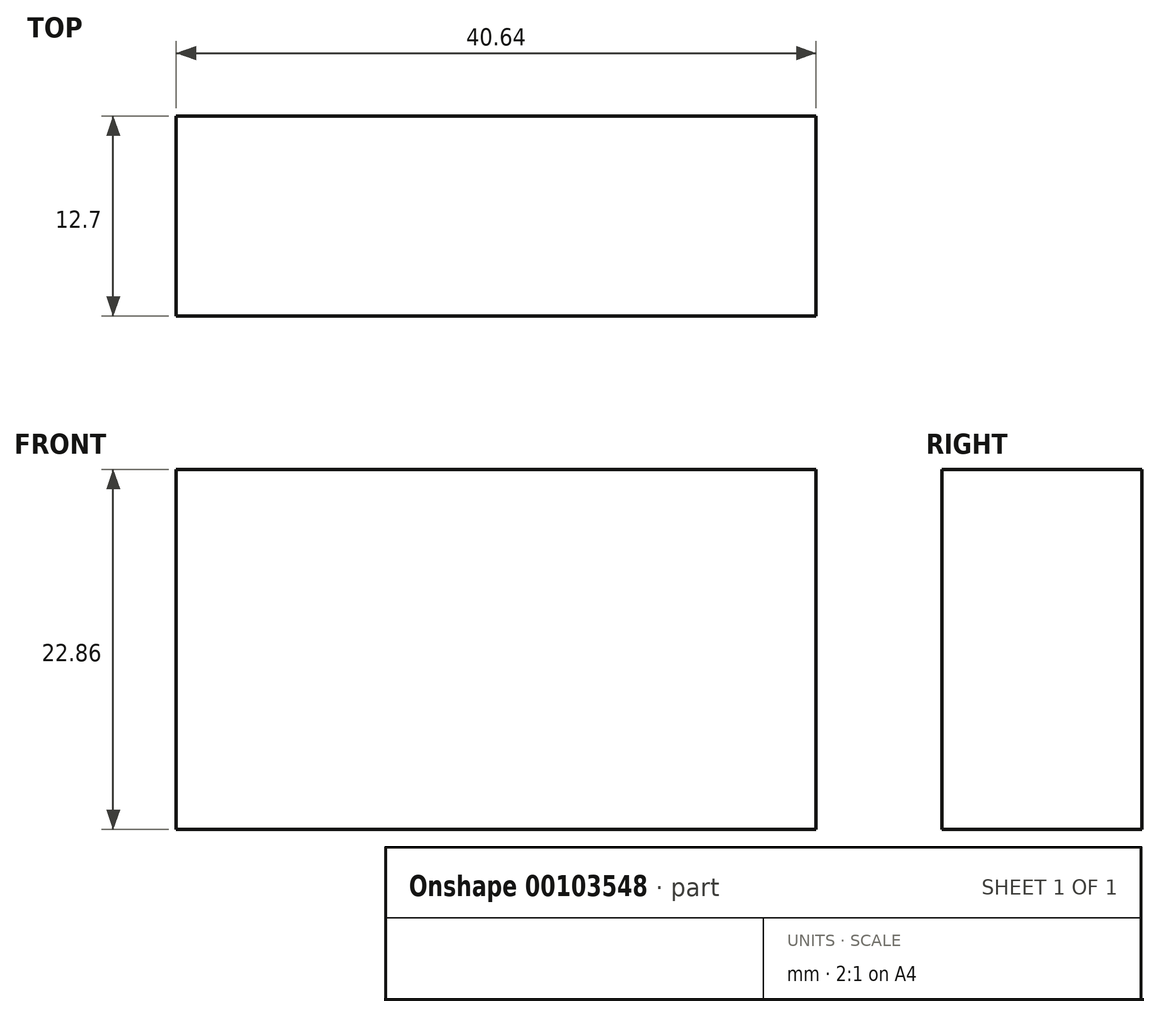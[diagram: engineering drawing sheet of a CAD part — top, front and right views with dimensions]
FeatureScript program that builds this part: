
annotation { "Feature Type Name" : "Feature", "Feature Type Description" : "" }
export const myFeature = defineFeature(function(context is Context, id is Id, definition is map)
    precondition{}
    {
        {
            var Q0;
            Q0=qCreatedBy(makeId("Front.planeOp"),FACE);
            var sketch = newSketch(context, id + "F0", { "sketchPlane" : qUnion([Q0])});
            skLineSegment(sketch, "E0.bottom", {"start": v(-59.18, 39.47) * mm, "end": v(-18.54, 39.47) * mm});
            skLineSegment(sketch, "E0.top", {"start": v(-59.18, 16.61) * mm, "end": v(-18.54, 16.61) * mm});
            skLineSegment(sketch, "E0.left", {"start": v(-59.18, 39.47) * mm, "end": v(-59.18, 16.61) * mm});
            skLineSegment(sketch, "E0.right", {"start": v(-18.54, 39.47) * mm, "end": v(-18.54, 16.61) * mm});
            skSolve(sketch);
        }
        {
            var Q0;
            Q0=makeQuery(id+"F0.imprint","IMPRINT",FACE,{"disambiguationData":[TD([[makeQuery(id+"F0.imprint","IMPRINT",EDGE,{"derivedFrom":sQuery(id+"F0.wireOp",EDGE,"E0.bottom")}),-1.0]])]});
            extrude(context, id + "F1", {"entities" : qUnion([Q0]), "depth" : 12.7 * mm});
        }
    });
